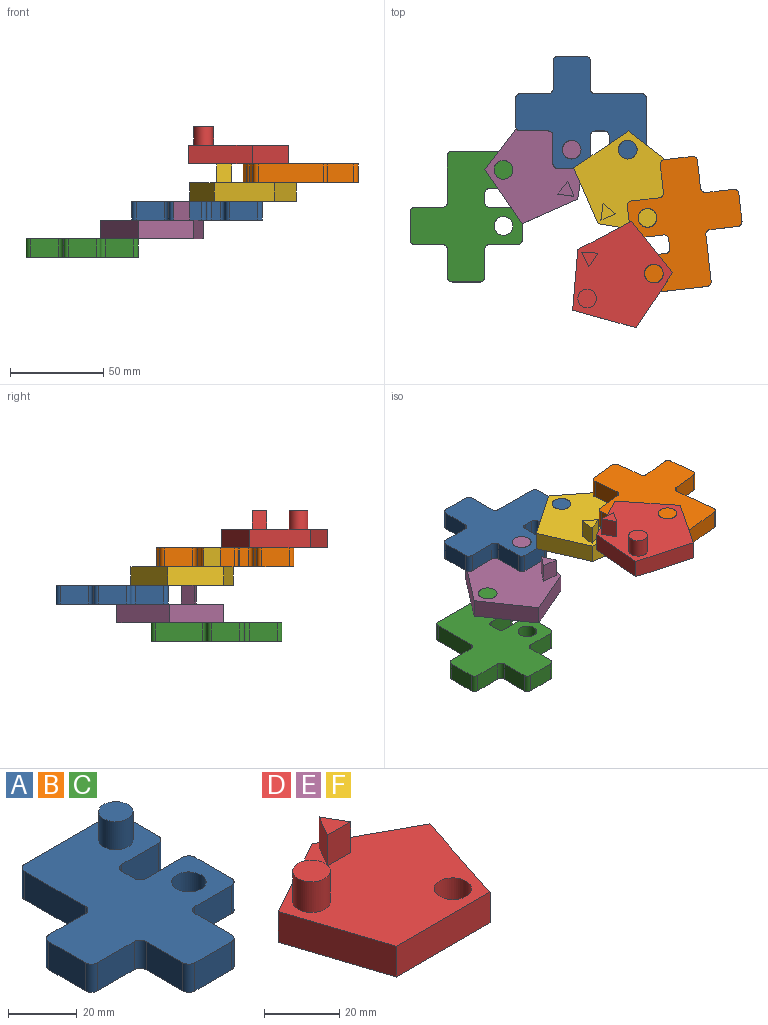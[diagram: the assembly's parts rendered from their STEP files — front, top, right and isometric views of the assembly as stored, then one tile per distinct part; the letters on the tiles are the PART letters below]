
ASSEMBLY  parts=6 mates=5
PART A: 33 faces, bbox 60x70x20 mm
  f0: cylinder r=2.5mm len=10mm, axis (0,0,-1), area 39.3mm2, adj f1,f28,f29,f30
  f1: plane 35x10mm, normal (0,1,0), area 350mm2, adj f0,f2,f29,f30
  f2: cylinder r=2.5mm len=10mm, axis (0,0,-1), area 39.3mm2, adj f1,f3,f29,f30
  f3: plane 25x10mm, normal (-1,0,0), area 250mm2, adj f2,f4,f29,f30
  f4: cylinder r=2.5mm len=10mm, axis (0,0,-1), area 39.3mm2, adj f3,f5,f29,f30
  f5: plane 15x10mm, normal (0,1,0), area 150mm2, adj f4,f6,f29,f30
  f6: cylinder r=2.5mm len=10mm, axis (0,0,-1), area 39.3mm2, adj f5,f7,f29,f30
  f7: plane 15x10mm, normal (-1,0,0), area 150mm2, adj f6,f8,f29,f30
  f8: cylinder r=2.5mm len=10mm, axis (0,0,-1), area 39.3mm2, adj f7,f9,f29,f30
  f9: plane 15x10mm, normal (0,-1,0), area 150mm2, adj f8,f10,f29,f30
  f10: cylinder r=2.5mm len=10mm, axis (0,0,-1), area 39.3mm2, adj f9,f11,f29,f30
  f11: plane 15x10mm, normal (-1,0,0), area 150mm2, adj f10,f12,f29,f30
  f12: cylinder r=2.5mm len=10mm, axis (0,0,-1), area 39.3mm2, adj f11,f13,f29,f30
  f13: plane 15x10mm, normal (0,-1,0), area 150mm2, adj f12,f14,f29,f30
  f14: cylinder r=2.5mm len=10mm, axis (0,0,-1), area 39.3mm2, adj f13,f15,f29,f30
  f15: plane 15x10mm, normal (1,0,0), area 150mm2, adj f14,f16,f29,f30
  f16: cylinder r=2.5mm len=10mm, axis (0,0,-1), area 39.3mm2, adj f15,f17,f29,f30
  f17: plane 15x10mm, normal (0,-1,0), area 150mm2, adj f16,f18,f29,f30
  f18: cylinder r=2.5mm len=10mm, axis (0,0,-1), area 39.3mm2, adj f17,f19,f29,f30
  f19: plane 15x10mm, normal (1,0,0), area 150mm2, adj f18,f20,f29,f30
  f20: cylinder r=2.5mm len=10mm, axis (0,0,-1), area 39.3mm2, adj f19,f21,f29,f30
  f21: plane 15x10mm, normal (0,1,0), area 150mm2, adj f20,f22,f29,f30
  f22: cylinder r=2.5mm len=10mm, axis (0,0,-1), area 39.3mm2, adj f21,f23,f29,f30
  f23: plane 10x5mm, normal (1,0,0), area 50mm2, adj f22,f24,f29,f30
  f24: cylinder r=2.5mm len=10mm, axis (0,0,-1), area 39.3mm2, adj f23,f25,f29,f30
  f25: plane 15x10mm, normal (0,-1,0), area 150mm2, adj f24,f26,f29,f30
  f26: cylinder r=2.5mm len=10mm, axis (0,0,-1), area 39.3mm2, adj f25,f28,f29,f30
  f27: cylinder r=5mm len=10mm, axis (0,0,-1), area 314.2mm2, adj f29,f30
  f28: plane 15x10mm, normal (1,0,0), area 150mm2, adj f0,f26,f29,f30
  f29: plane 70x60mm, normal (0,0,1), area 2437.6mm2, adj f0,f1,f2,f3,f4,f5,f6,f7
  f30: plane 70x60mm, normal (0,0,-1), area 2516.1mm2, adj f0,f1,f2,f3,f4,f5,f6,f7
  f31: cylinder r=5mm len=10mm, axis (0,0,-1), area 314.2mm2, adj f29,f32
  f32: plane 10x10mm, normal (0,0,1), area 78.5mm2, adj f31
PART B: same geometry as A
PART C: same geometry as A
PART D: 14 faces, bbox 57.1x49.1x20 mm
  f0: plane 28.53x15.56mm, normal (-0.48,0.88,0), area 325mm2, adj f1,f5,f6,f7
  f1: plane 33.54x10.9mm, normal (-0.95,-0.31,0), area 352.7mm2, adj f0,f2,f6,f7
  f2: plane 35.27x10mm, normal (0,-1,0), area 352.7mm2, adj f1,f3,f6,f7
  f3: plane 33.54x10.9mm, normal (0.95,-0.31,0), area 352.7mm2, adj f2,f5,f6,f7
  f4: cylinder r=5mm len=10mm, axis (0,0,-1), area 314.2mm2, adj f6,f7
  f5: plane 28.53x15.56mm, normal (0.48,0.88,0), area 325mm2, adj f0,f3,f6,f7
  f6: plane 57.06x49.1mm, normal (0,0,1), area 1802.9mm2, adj f0,f1,f2,f3,f4,f5,f8,f11
  f7: plane 57.06x49.1mm, normal (0,0,-1), area 1913.9mm2, adj f0,f1,f2,f3,f4,f5
  f8: cylinder r=5mm len=10mm, axis (0,0,-1), area 314.2mm2, adj f6,f9
  f9: plane 10x10mm, normal (0,0,1), area 78.5mm2, adj f8
  f10: plane 8.66x7.5mm, normal (0,0,1), area 32.5mm2, adj f11,f12,f13
  f11: plane 10x7.5mm, normal (-0.87,0.5,0), area 86.6mm2, adj f6,f10,f12,f13
  f12: plane 10x7.5mm, normal (0.87,0.5,0), area 86.6mm2, adj f6,f10,f11,f13
  f13: plane 10x8.66mm, normal (0,-1,0), area 86.6mm2, adj f6,f10,f11,f12
PART E: same geometry as D
PART F: same geometry as D
PLACE A rot(axis=(0,0,-1),90.1deg) t=(210.43,102.59,11.65)mm
PLACE B rot(axis=(0,0,-1),173.5deg) t=(270.86,48.28,31.65)mm
PLACE C t=(153.92,41.83,-8.35)mm fixed
PLACE D rot(axis=(0,0,1),56.5deg) t=(234.4,15.35,41.65)mm
PLACE E rot(axis=(0,0,-1),127.6deg) t=(193.91,71.28,1.65)mm
PLACE F rot(axis=(0,0,1),142.1deg) t=(239.76,62.57,21.65)mm
MATE revolute C.f31 <-> E.f4  axis (0,0,1) through (173.92,71.83,11.65)mm
MATE revolute F.f8 <-> B.f27  axis (0,0,1) through (250.99,46.02,41.65)mm
MATE revolute E.f8 <-> A.f27  axis (0,0,1) through (210.41,82.59,21.65)mm
MATE revolute B.f31 <-> D.f4  axis (0,0,1) through (254.39,16.21,51.65)mm
MATE revolute A.f31 <-> F.f4  axis (0,0,1) through (240.41,82.56,31.65)mm
